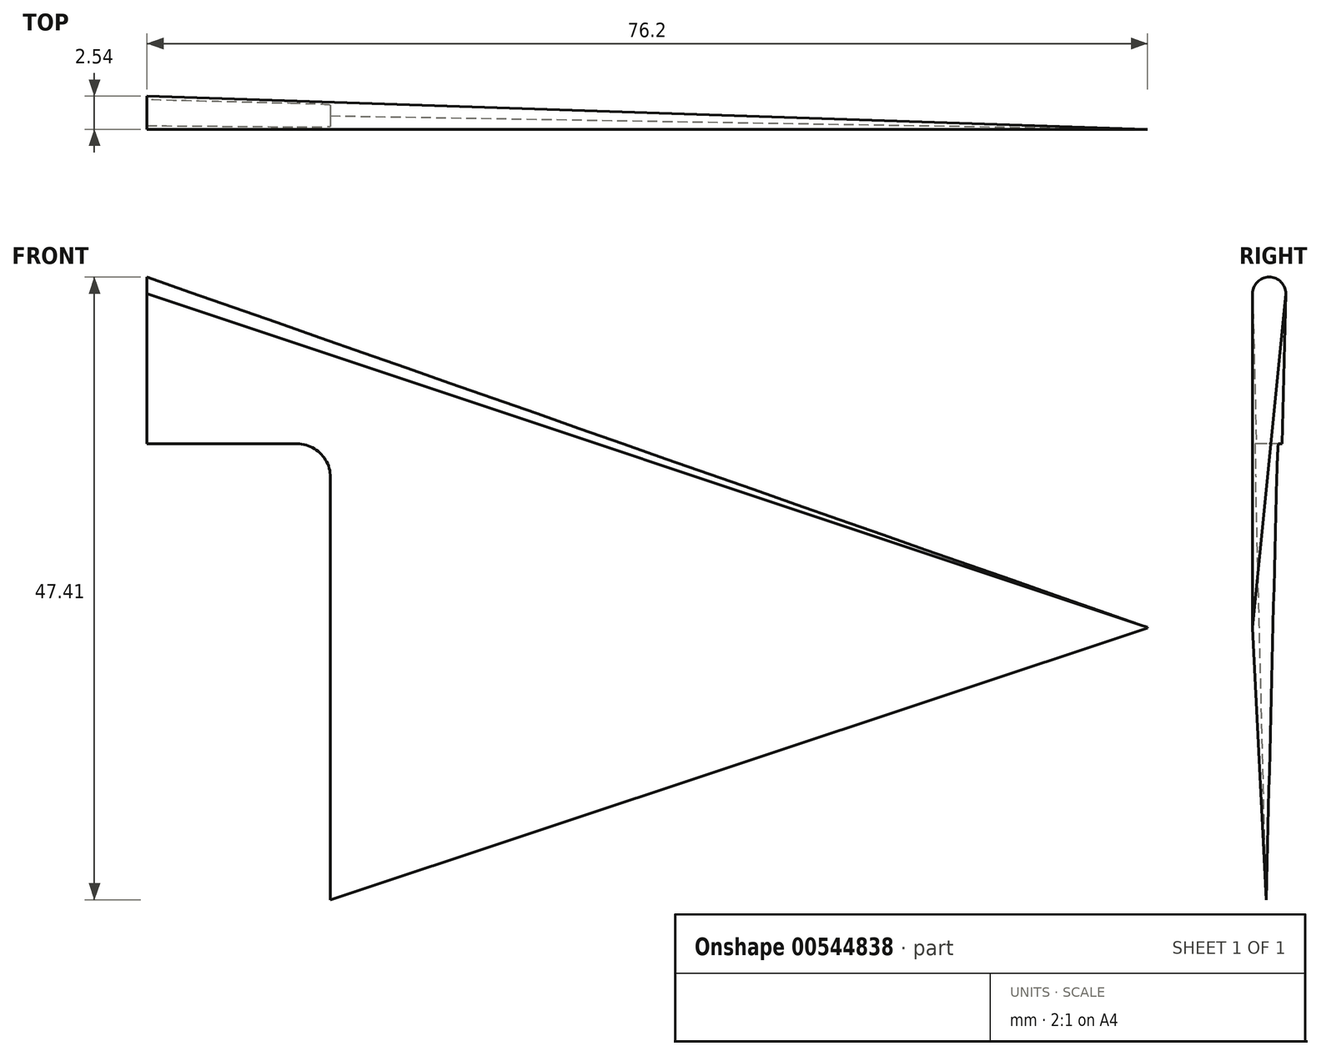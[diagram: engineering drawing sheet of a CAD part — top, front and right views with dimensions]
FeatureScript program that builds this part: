
annotation { "Feature Type Name" : "Feature", "Feature Type Description" : "" }
export const myFeature = defineFeature(function(context is Context, id is Id, definition is map)
    precondition{}
    {
        {
            var Q0;
            Q0=qCreatedBy(makeId("Right.planeOp"),FACE);
            var sketch = newSketch(context, id + "F0", { "sketchPlane" : qUnion([Q0])});
            skLineSegment(sketch, "E0", {"start": v(0, 0) * mm, "end": v(1.27, 50.78) * mm});
            skArc(sketch, "E1", {"start": v(1.27, 50.72) * mm, "mid": v(0, 52.05) * mm, "end": v(-1.27, 50.72) * mm});
            skLineSegment(sketch, "E2", {"start": v(-1.27, 50.78) * mm, "end": v(0, 0) * mm});
            skSolve(sketch);
        }
        {
            var Q0;
            Q0=qCreatedBy(makeId("Right.planeOp"),FACE);
            cPlane(context, id + "F1", {"entities" : qUnion([Q0]), "cplaneType" : CPlaneType.OFFSET, "offset" : 76.2 * mm, "width" : 152.4 * mm, "height" : 152.4 * mm});
        }
        {
            var Q0;
            Q0=qCreatedBy(id+"F1.planeOp",FACE);
            var sketch = newSketch(context, id + "F2", { "sketchPlane" : qUnion([Q0])});
            skLineSegment(sketch, "E3", {"start": v(0, -25.4) * mm, "end": v(1.27, 25.38) * mm});
            skArc(sketch, "E4", {"start": v(1.27, 25.35) * mm, "mid": v(-0.02, 26.65) * mm, "end": v(-1.27, 25.32) * mm});
            skLineSegment(sketch, "E5", {"start": v(-1.27, 25.38) * mm, "end": v(0, -25.4) * mm});
            skSolve(sketch);
        }
        {
            var Q0;
            {var subQ0=sQuery(id+"F0.wireOp",EDGE,"E0");Q0=makeQuery(id+"F0.imprint","IMPRINT",FACE,{"disambiguationData":[TD([[makeQuery(id+"F0.imprint","IMPRINT",EDGE,{"derivedFrom":subQ0}),1.0]])]});}
            var Q1;
            {var subQ3=sQuery(id+"F2.wireOp",EDGE,"E4");Q1=makeQuery(id+"F2.imprint","IMPRINT",FACE,{"disambiguationData":[TD([[makeQuery(id+"F2.imprint","IMPRINT",EDGE,{"derivedFrom":subQ3}),1.0]])]});}
            loft(context, id + "F3", {"sheetProfilesArray" : [{ "sheetProfileEntities" : qUnion([Q0]) }, { "sheetProfileEntities" : qUnion([Q1]) }]});
        }
        {
            var Q0;
            Q0=qCreatedBy(makeId("Front.planeOp"),FACE);
            var sketch = newSketch(context, id + "F4", { "sketchPlane" : qUnion([Q0])});
            skLineSegment(sketch, "E6.bottom", {"start": v(0, -7.92) * mm, "end": v(13.97, -7.92) * mm});
            skLineSegment(sketch, "E6.top", {"start": v(0, 39.35) * mm, "end": v(13.97, 39.35) * mm});
            skLineSegment(sketch, "E6.left", {"start": v(0, -7.92) * mm, "end": v(0, 39.35) * mm});
            skLineSegment(sketch, "E6.right", {"start": v(13.97, -7.92) * mm, "end": v(13.97, 39.35) * mm});
            skPoint(sketch, "E7.0", {"position": v(0, 52.05) * mm});
            skSolve(sketch);
        }
        {
            var Q0;
            Q0 = qSketchRegion(id + "F4", true);
            extrude(context, id + "F5", {"entities" : qUnion([Q0]), "operationType" : NewBodyOperationType.REMOVE, "endBound" : BoundingType.SYMMETRIC, "oppositeDirection" : true, "depth" : 25.4 * mm, "offsetDistance" : 25.4 * mm});
        }
        {
            var Q0;
            Q0=makeQuery(id+"F5.boolean.opBoolean","COPY",EDGE,{"derivedFrom":makeQuery(id+"F5.opExtrude","SWEPT_EDGE",EDGE,{"disambiguationData":[OSD([sQuery(id+"F4.wireOp",EDGE,"E6.top"),sQuery(id+"F4.wireOp",EDGE,"E6.right")])]})});
            fillet(context, id + "F6", {"entities" : qUnion([Q0]), "radius" : 2.54 * mm, "tangentPropagation" : true, "allowEdgeOverflow" : false});
        }
    });
